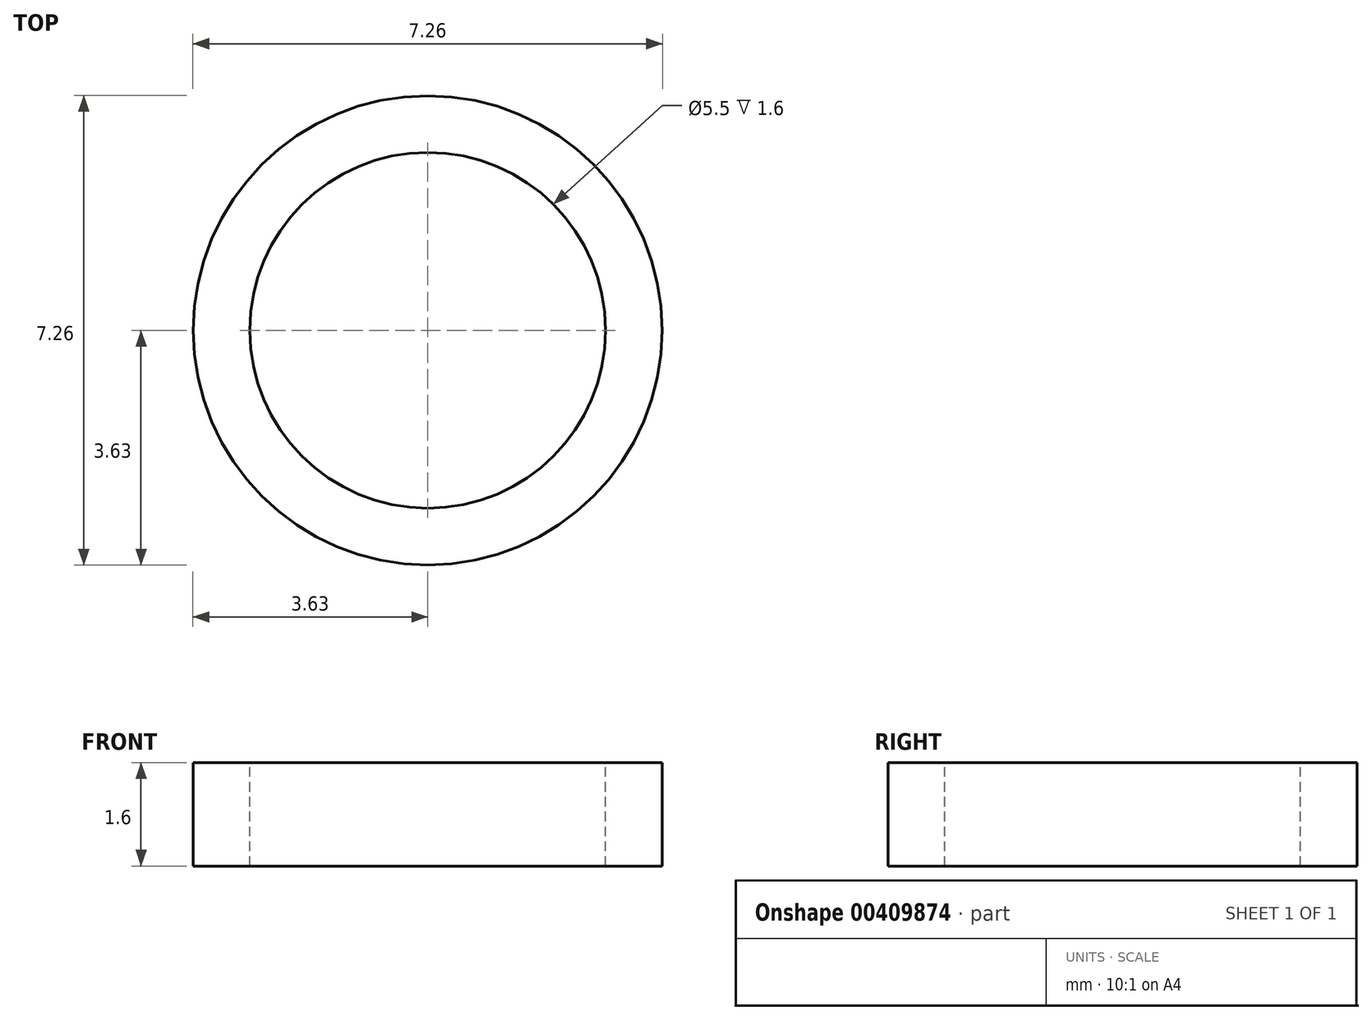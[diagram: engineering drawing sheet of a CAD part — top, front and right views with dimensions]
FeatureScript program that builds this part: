
annotation { "Feature Type Name" : "Feature", "Feature Type Description" : "" }
export const myFeature = defineFeature(function(context is Context, id is Id, definition is map)
    precondition{}
    {
        {
            var Q0;
            Q0=qCreatedBy(makeId("Top.planeOp"),FACE);
            var sketch = newSketch(context, id + "F0", { "sketchPlane" : qUnion([Q0])});
            skCircle(sketch, "E0", {"center": v(0, 0) * mm, "radius": 3.63 * mm});
            skSolve(sketch);
        }
        {
            var Q0;
            Q0=qSketchRegion(id+"F0",true);
            extrude(context, id + "F1", {"entities" : qUnion([Q0]), "endBound" : BoundingType.SYMMETRIC, "depth" : 1.6 * mm});
        }
        {
            var Q0;
            Q0=qCreatedBy(makeId("Top.planeOp"),FACE);
            var sketch = newSketch(context, id + "F2", { "sketchPlane" : qUnion([Q0])});
            skCircle(sketch, "E1", {"center": v(0, 0) * mm, "radius": 2.75 * mm});
            skSolve(sketch);
        }
        {
            var Q0;
            Q0=qSketchRegion(id+"F2",true);
            extrude(context, id + "F3", {"entities" : qUnion([Q0]), "operationType" : NewBodyOperationType.REMOVE, "endBound" : BoundingType.THROUGH_ALL, "oppositeDirection" : true, "depth" : 25 * mm, "hasSecondDirection" : true, "secondDirectionBound" : SecondDirectionBoundingType.THROUGH_ALL, "secondDirectionOppositeDirection" : false, "secondDirectionDepth" : 25 * mm});
        }
    });
